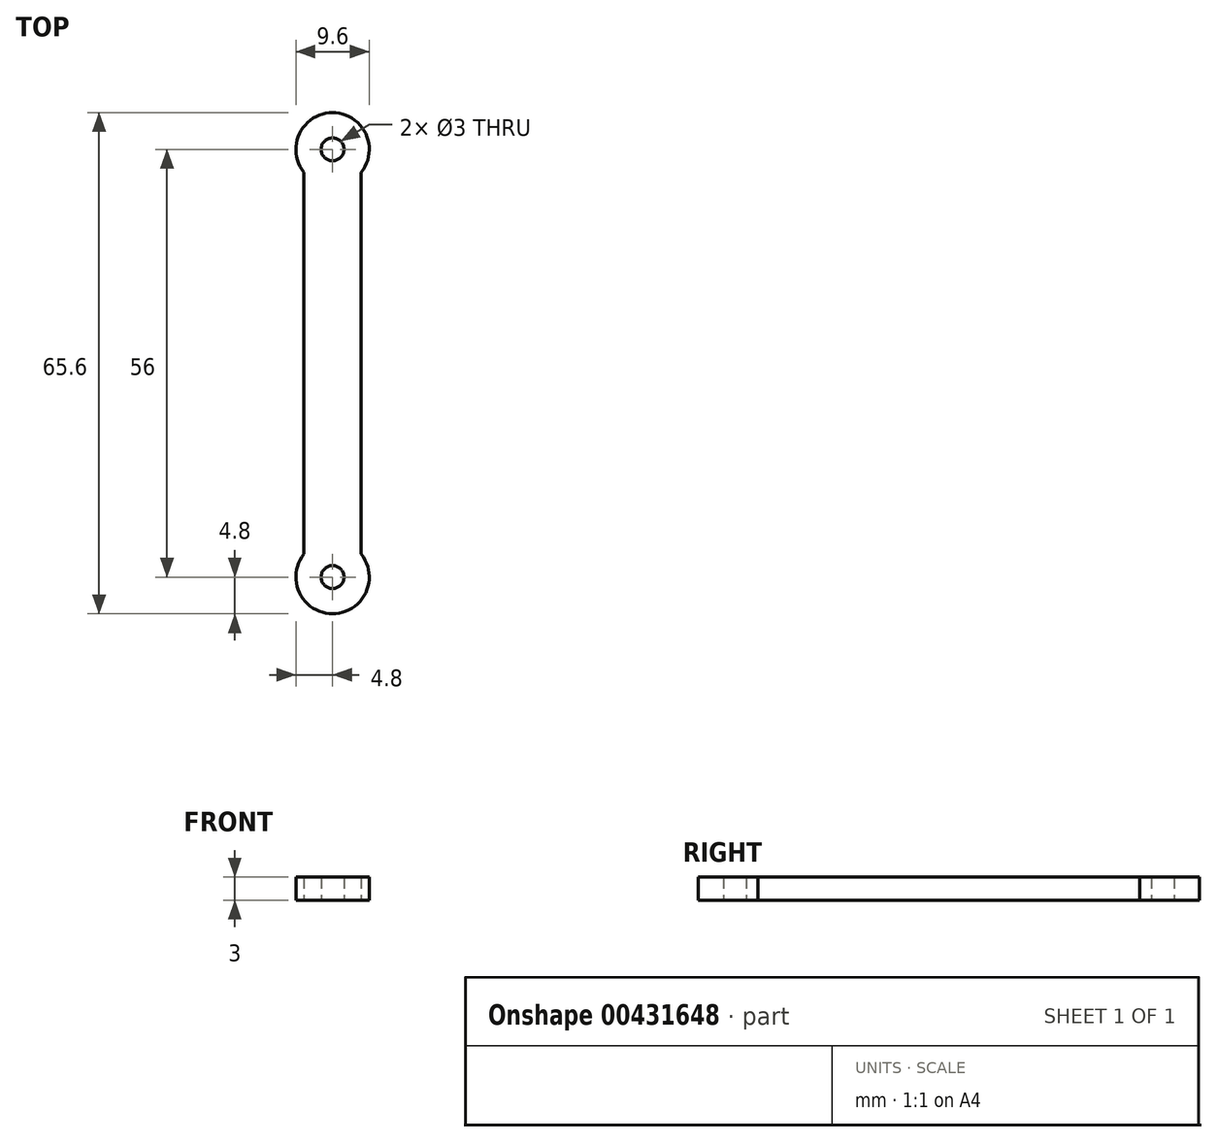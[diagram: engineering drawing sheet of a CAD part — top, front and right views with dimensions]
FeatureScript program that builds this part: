
annotation { "Feature Type Name" : "Feature", "Feature Type Description" : "" }
export const myFeature = defineFeature(function(context is Context, id is Id, definition is map)
    precondition{}
    {
        {
            var Q0;
            Q0=qCreatedBy(makeId("Top.planeOp"),FACE);
            var sketch = newSketch(context, id + "F0", { "sketchPlane" : qUnion([Q0])});
            skLineSegment(sketch, "E0.bottom", {"start": v(0, 0) * mm, "end": v(7.5, 0) * mm, "construction": true});
            skLineSegment(sketch, "E0.top", {"start": v(0, 50) * mm, "end": v(7.5, 50) * mm, "construction": true});
            skLineSegment(sketch, "E0.left", {"start": v(0, 0) * mm, "end": v(0, 50) * mm});
            skLineSegment(sketch, "E0.right", {"start": v(7.5, 0) * mm, "end": v(7.5, 50) * mm});
            skLineSegment(sketch, "E1", {"start": v(3.75, 0) * mm, "end": v(3.75, -3) * mm, "construction": true});
            skArc(sketch, "E2", {"start": v(0, 0) * mm, "mid": v(3.75, -7.8) * mm, "end": v(7.5, 0) * mm});
            skArc(sketch, "E3", {"start": v(7.5, 0) * mm, "mid": v(3.75, 1.8) * mm, "end": v(0, 0) * mm, "construction": true});
            skCircle(sketch, "E4", {"center": v(3.75, -3) * mm, "radius": 1.5 * mm});
            skLineSegment(sketch, "E5", {"start": v(3.75, 50) * mm, "end": v(3.75, 53) * mm, "construction": true});
            skCircle(sketch, "E6", {"center": v(3.75, 53) * mm, "radius": 1.5 * mm});
            skArc(sketch, "E7", {"start": v(0, 50) * mm, "mid": v(3.75, 48.2) * mm, "end": v(7.5, 50) * mm, "construction": true});
            skArc(sketch, "E8", {"start": v(7.5, 50) * mm, "mid": v(3.75, 57.8) * mm, "end": v(0, 50) * mm});
            skSolve(sketch);
        }
        {
            var Q0;
            Q0=makeQuery(id+"F0.imprint","IMPRINT",FACE,{"disambiguationData":[TD([[makeQuery(id+"F0.imprint","IMPRINT",EDGE,{"derivedFrom":sQuery(id+"F0.wireOp",EDGE,"E0.left")}),-1.0]])]});
            extrude(context, id + "F1", {"entities" : qUnion([Q0]), "depth" : 3 * mm});
        }
    });
